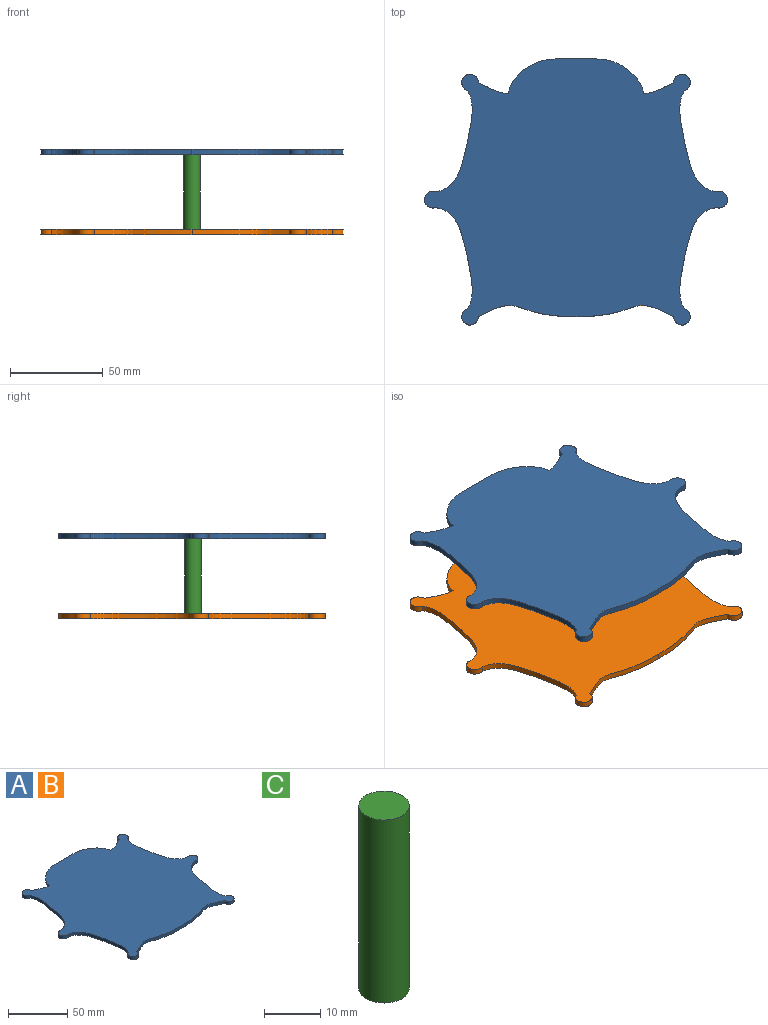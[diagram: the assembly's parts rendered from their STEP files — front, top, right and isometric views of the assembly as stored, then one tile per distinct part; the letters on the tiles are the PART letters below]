
ASSEMBLY  parts=3 mates=2
PART A: 20 faces, bbox 163x143.2x3 mm
  f0: extruded ~54.43x19.76mm, area 187.8mm2, adj f1,f17,f18,f19
  f1: cylinder r=4.5mm len=9mm, axis (0,0,-1), area 50.7mm2, adj f0,f2,f18,f19
  f2: extruded ~54.43x19.76mm, area 187.8mm2, adj f1,f3,f18,f19
  f3: cylinder r=4.49mm len=8.98mm, axis (0,0,-1), area 59.3mm2, adj f2,f4,f18,f19
  f4: extruded ~52.51x6.1mm, area 163.5mm2, adj f3,f5,f18,f19
  f5: extruded ~52.51x6.1mm, area 163.5mm2, adj f4,f6,f18,f19
  f6: cylinder r=4.49mm len=8.98mm, axis (0,0,-1), area 59.3mm2, adj f5,f7,f18,f19
  f7: extruded ~54.43x19.76mm, area 187.8mm2, adj f6,f8,f18,f19
  f8: cylinder r=4.5mm len=9mm, axis (0,0,-1), area 50.7mm2, adj f7,f9,f18,f19
  f9: extruded ~54.43x19.76mm, area 187.8mm2, adj f8,f10,f18,f19
  f10: cylinder r=4.49mm len=8.98mm, axis (0,0,-1), area 59.3mm2, adj f9,f11,f18,f19
  f11: extruded ~16.24x6.1mm, area 52.4mm2, adj f10,f12,f18,f19
  f12: extruded ~26.23x18.86mm, area 105.4mm2, adj f11,f13,f18,f19
  f13: plane 20.08x3mm, normal (0,1,0), area 60.2mm2, adj f12,f14,f18,f19
  f14: extruded ~24.25x12.76mm, area 85.9mm2, adj f13,f15,f18,f19
  f15: extruded ~6.1x3mm, area 19.5mm2, adj f14,f16,f18,f19
  f16: extruded ~16.24x6.1mm, area 52.4mm2, adj f15,f17,f18,f19
  f17: cylinder r=4.49mm len=8.98mm, axis (0,0,-1), area 59.3mm2, adj f0,f16,f18,f19
  f18: plane 163x143.25mm, normal (0,0,1), area 15855.6mm2, adj f0,f1,f2,f3,f4,f5,f6,f7
  f19: plane 163x143.25mm, normal (0,0,-1), area 15855.6mm2, adj f0,f1,f2,f3,f4,f5,f6,f7
PART B: same geometry as A
PART C: 3 faces, bbox 9x9x40 mm
  f0: cylinder r=4.5mm len=40mm, axis (0,0,-1), area 1131mm2, adj f1,f2
  f1: plane 9x9mm, normal (0,0,1), area 63.6mm2, adj f0
  f2: plane 9x9mm, normal (0,0,-1), area 63.6mm2, adj f0
PLACE A t=(0,0,43)mm
PLACE B at identity
PLACE C t=(0,2.64,3)mm
MATE fastened A.f19 <-> C.f0  axis (0,0,-1) through (0,3.61,43)mm
MATE fastened C.f0 <-> B.f18  axis (0,0,-1) through (0,3.61,3)mm
